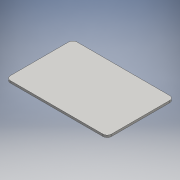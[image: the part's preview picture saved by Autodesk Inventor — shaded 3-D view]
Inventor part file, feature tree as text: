
AUTODESK INVENTOR PART (.ipt)
format: ipt  version: 2016 (Build 200138000, 138)  size: 115,712 bytes
history: native  units: mm
features: extrude x2, sketch x2
ambient origin geometry x8: Origin, YZ Plane, XZ Plane, XY Plane, X Axis, Y Axis, Z Axis, Center Point
bodies: Solid1 (feature_tree)
feature tree (4):
  extrude  "Extrusion1"  Depth=159.5mm
  extrude  "Extrusion2"  Depth=5.0mm
  sketch  "Sketch1"  dims[d0=159.5mm d1=79.75mm]
  sketch  "Sketch2"  dims[d2=109.5mm d3=54.75mm d4=4.0mm d5=3.0mm d6=0.0mm d7=238.2mm d8=157.2mm d9=119.1mm d10=78.6mm d11=10.0mm d12=5.0mm d13=0.0mm]
